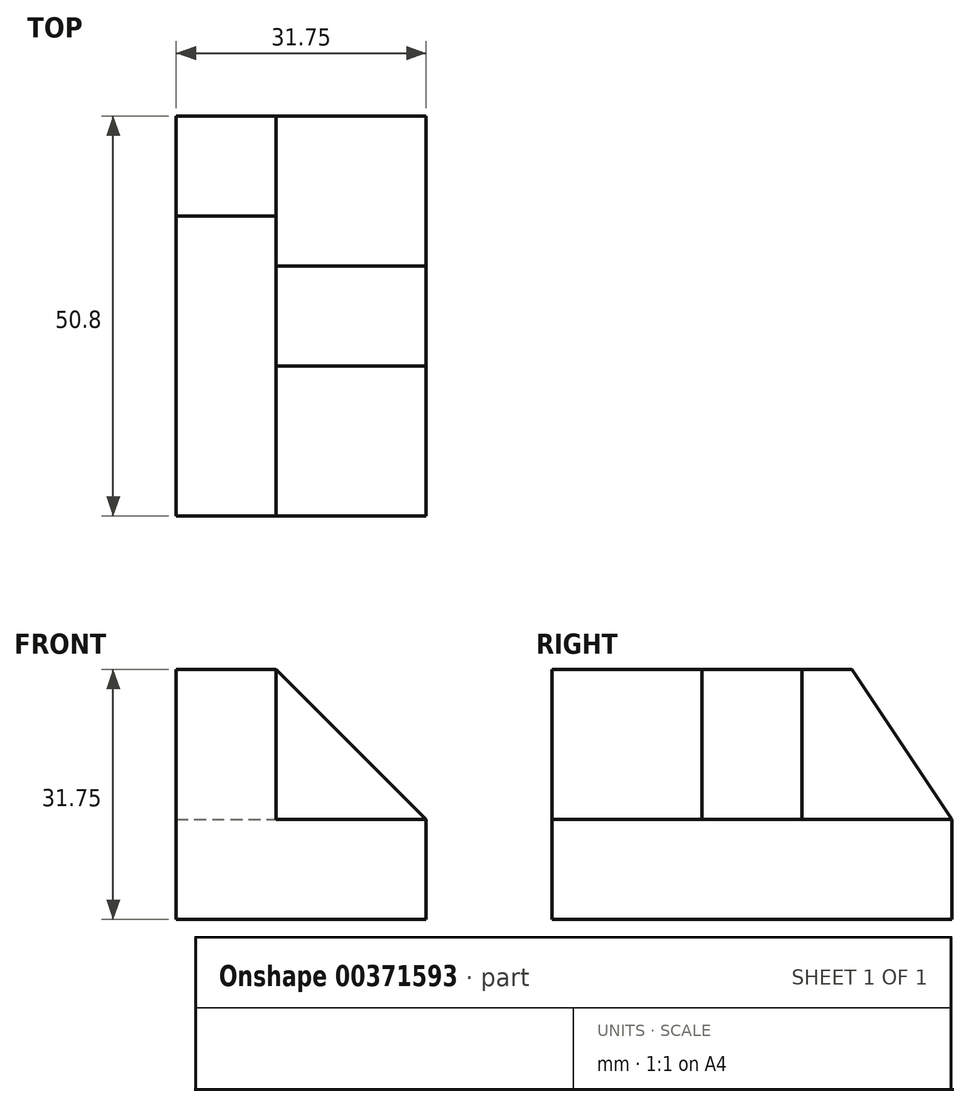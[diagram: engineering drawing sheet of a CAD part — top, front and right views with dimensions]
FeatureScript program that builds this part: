
annotation { "Feature Type Name" : "Feature", "Feature Type Description" : "" }
export const myFeature = defineFeature(function(context is Context, id is Id, definition is map)
    precondition{}
    {
        {
            var Q0;
            Q0=qCreatedBy(makeId("Front.planeOp"),FACE);
            var sketch = newSketch(context, id + "F0", { "sketchPlane" : qUnion([Q0])});
            skLineSegment(sketch, "E0", {"start": v(0, 0) * mm, "end": v(0, 19.05) * mm});
            skLineSegment(sketch, "E1", {"start": v(0, 19.05) * mm, "end": v(-12.7, 19.05) * mm});
            skLineSegment(sketch, "E2", {"start": v(-12.7, 19.05) * mm, "end": v(-12.7, -12.7) * mm});
            skLineSegment(sketch, "E3", {"start": v(-12.7, -12.7) * mm, "end": v(19.05, -12.7) * mm});
            skLineSegment(sketch, "E4", {"start": v(19.05, -12.7) * mm, "end": v(19.05, 0) * mm});
            skLineSegment(sketch, "E5", {"start": v(19.05, 0) * mm, "end": v(0, 0) * mm});
            skSolve(sketch);
        }
        {
            var Q0;
            Q0=makeQuery(id+"F0.imprint","IMPRINT",FACE,{"disambiguationData":[TD([[makeQuery(id+"F0.imprint","IMPRINT",EDGE,{"derivedFrom":sQuery(id+"F0.wireOp",EDGE,"E0")}),1.0]])]});
            extrude(context, id + "F1", {"entities" : qUnion([Q0]), "depth" : 50.8 * mm});
        }
        {
            var Q0;
            Q0=makeQuery(id+"F1.opExtrude","SWEPT_FACE",FACE,{"disambiguationData":[OSD([sQuery(id+"F0.wireOp",EDGE,"E0")])]});
            var sketch = newSketch(context, id + "F2", { "sketchPlane" : qUnion([Q0])});
            skLineSegment(sketch, "E6", {"start": v(-12.7, 19.05) * mm, "end": v(0, 0) * mm});
            skSolve(sketch);
        }
        {
            var Q0;
            {var subQ0=sQuery(id+"F2.wireOp",EDGE,"E6");Q0=makeQuery(id+"F2.imprint","IMPRINT",FACE,{"disambiguationData":[TD([[makeQuery(id+"F2.imprint","IMPRINT",EDGE,{"derivedFrom":subQ0}),1.0]])]});}
            extrude(context, id + "F3", {"entities" : qUnion([Q0]), "operationType" : NewBodyOperationType.REMOVE, "oppositeDirection" : true, "depth" : 25.4 * mm});
        }
        {
            var Q0;
            Q0=makeQuery(id+"F1.opExtrude","SWEPT_FACE",FACE,{"disambiguationData":[OSD([sQuery(id+"F0.wireOp",EDGE,"E5")])]});
            var sketch = newSketch(context, id + "F4", { "sketchPlane" : qUnion([Q0])});
            skLineSegment(sketch, "E7", {"start": v(19.05, -19.05) * mm, "end": v(0, -19.05) * mm});
            skLineSegment(sketch, "E8", {"start": v(19.05, -31.75) * mm, "end": v(0, -31.75) * mm});
            skSolve(sketch);
        }
        {
            var Q0;
            {var subQ0=sQuery(id+"F4.wireOp",EDGE,"E7");Q0=makeQuery(id+"F4.imprint","IMPRINT",FACE,{"disambiguationData":[TD([[makeQuery(id+"F4.imprint","IMPRINT",EDGE,{"derivedFrom":subQ0}),1.0]])]});}
            extrude(context, id + "F5", {"entities" : qUnion([Q0]), "operationType" : NewBodyOperationType.ADD, "depth" : 19.05 * mm});
        }
        {
            var Q0;
            Q0=makeQuery(id+"F5.opExtrude","SWEPT_FACE",FACE,{"disambiguationData":[OSD([sQuery(id+"F4.wireOp",EDGE,"E7")])]});
            var sketch = newSketch(context, id + "F6", { "sketchPlane" : qUnion([Q0])});
            skLineSegment(sketch, "E9", {"start": v(0, 19.05) * mm, "end": v(-19.05, 0) * mm});
            skSolve(sketch);
        }
        {
            var Q0;
            Q0=makeQuery(id+"F6.imprint","IMPRINT",FACE,{"disambiguationData":[TD([[makeQuery(id+"F6.imprint","IMPRINT",EDGE,{"derivedFrom":sQuery(id+"F6.wireOp",EDGE,"E9")}),-1.0]])]});
            extrude(context, id + "F7", {"entities" : qUnion([Q0]), "operationType" : NewBodyOperationType.REMOVE, "oppositeDirection" : true, "depth" : 25.4 * mm});
        }
    });
